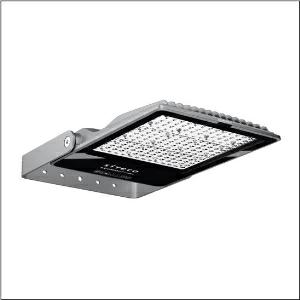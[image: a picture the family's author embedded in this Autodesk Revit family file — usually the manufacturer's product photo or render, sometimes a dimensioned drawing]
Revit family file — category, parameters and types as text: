
# Revit family: sicompact_r__31_midi___pl32_5xa7581e1k23_f752
name_source: partatom
category: Lighting Fixtures
units: mm (PartAtom-declared; Revit-internal decimal feet)

## family parameters
Cut with Voids When Loaded = No
Host = Face
Light Source = No
Part Type = Normal
Room Calculation Point = No
Round Connector Dimension = Use Diameter
Shared = No

## types (1)
- SiCompact® 31 midi  PL32 (1 x LED, 37000 lm, 250 W, 3000K)
    Apparent Load = 250 VA
    CIE Flux Codes = 32 69 98 100 100
    Color Rendering = 70
    Color Temperature = 3000K
    Default Elevation = 1800 mm
    Description = SiCompact® 31 midi, floodlight, primary light control with lens, of plastic, of toughened safety glass, transparent, light distribution: PL32, light emission: direct distribution, primary light characteristic: asymmetric, installation type: surface-mounted, LED, High Power LED, rated luminous flux: 37.000lm, luminous efficacy: 148lm/W, light colour: 730, colour temperature: 3000K, control gear: ECG, with cable, 3x 1.5mm², mains connection: 220..240V, AC, 50/60Hz, connection cable pre-assembled, cable length: 2m, rated input power: 250W, of diecast aluminium, specular, metallic grey (RAL 9006), length: 560mm, width: 330mm, height: 62mm, bracket, of sheet steel, coated, metallic grey (RAL 9006), ON/OFF, protection rating (complete): IP66, insulation class (complete): insulation class I (protective earthing), certification: CE, ENEC, impact resistance: IK08, permissible operating ambient temperature: -40..+45°C, packaging unit: 1 piece

Light Distribution: PL32
    Height = 62 mm  [stored 0.203412 ft]
    Lamp = 1 x LED
    Lamp Light Flux = 37000 lm
    Lamp Power = 250 W
    Lamp count = 1
    Length = 560 mm
    Luminous efficacy = 148 lm/W
    Manufacturer = Siteco
    ModVariant = No
    Model = 5XA7581E1K23
    Mounting Place = Wall
    Mounting Type = Surface mounted
    Number of Poles = 1
    OnlyDefault = Yes
    Power Factor = 1
    Product Name = SiCompact® 31 midi | PL32
    Product group = floodlight | wall mounted
    ProductGroupID = 2001
    Protection Class = Protection class I
    Protection Degree = IP 66
    RLX_Detail_Level = 1
    RLX_Emergency_Light_Flux = 0 lm
    RLX_Emergency_Type = 0
    RLX_Emergency_Type_DB = No
    RlxData = <blob elided: 98129 chars, md5=8b45d70e>
    Socket = socket
    Standby Power = 0 W
    System Light Flux = 37000 lm
    System Power = 250 W
    Type Comments = Product without accessories
    Type Image = l_1006415.jpg
    URL = http://relux.com
    VarID = ---
    Voltage = 0 V
    Weight = 0.00 kg
    Width = 333 mm

note: [stored X ft] marks values corroborated as IEEE doubles in the binary element streams (Revit-internal decimal feet)

## geometry (parser evidence)
native form markers: Blend x4, Sweep x13
no freeform markers — native parametric forms only
